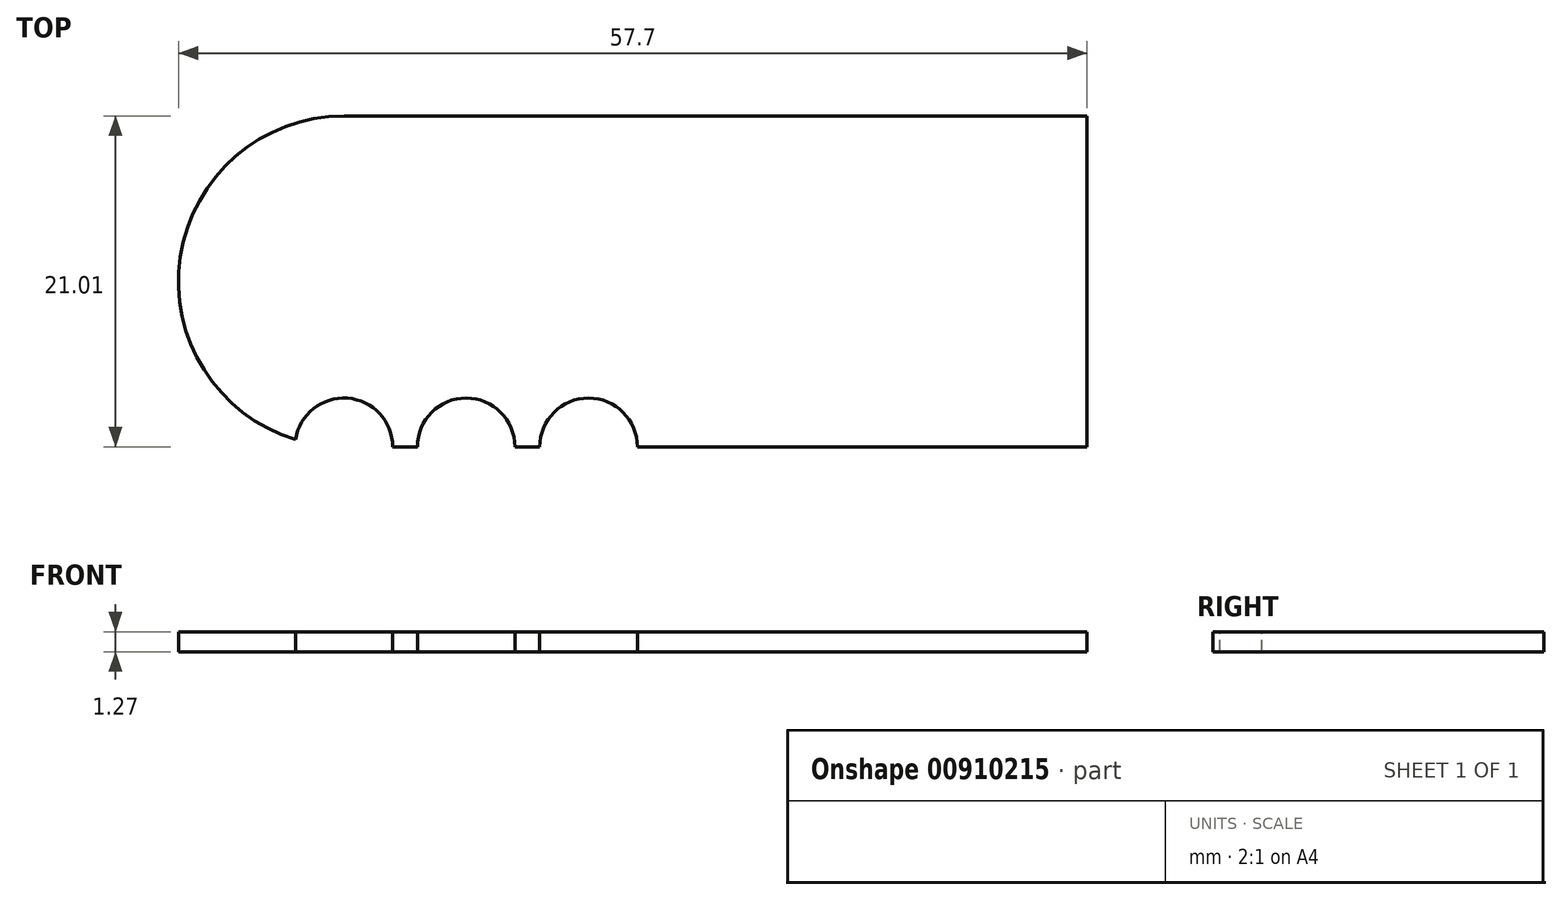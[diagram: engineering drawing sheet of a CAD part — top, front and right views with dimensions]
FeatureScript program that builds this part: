
annotation { "Feature Type Name" : "Feature", "Feature Type Description" : "" }
export const myFeature = defineFeature(function(context is Context, id is Id, definition is map)
    precondition{}
    {
        {
            var Q0;
            Q0=qCreatedBy(makeId("Top.planeOp"),FACE);
            var sketch = newSketch(context, id + "F0", { "sketchPlane" : qUnion([Q0])});
            skLineSegment(sketch, "E0.bottom", {"start": v(-3.6, 16.26) * mm, "end": v(43.6, 16.26) * mm});
            skLineSegment(sketch, "E0.top", {"start": v(-3.6, -4.75) * mm, "end": v(43.6, -4.75) * mm});
            skLineSegment(sketch, "E0.left", {"start": v(-3.6, 16.26) * mm, "end": v(-3.6, -4.75) * mm});
            skLineSegment(sketch, "E0.right", {"start": v(43.6, 16.26) * mm, "end": v(43.6, -4.75) * mm});
            skArc(sketch, "E1", {"start": v(-3.6, 16.26) * mm, "mid": v(-14.1, 5.76) * mm, "end": v(-3.6, -4.75) * mm});
            skSolve(sketch);
        }
        {
            var Q0;
            Q0=makeQuery(id+"F0.imprint","IMPRINT",FACE,{"disambiguationData":[TD([[makeQuery(id+"F0.imprint","IMPRINT",EDGE,{"derivedFrom":sQuery(id+"F0.wireOp",EDGE,"E0.bottom")}),-1.0]])]});
            var Q1;
            Q1=makeQuery(id+"F0.imprint","IMPRINT",FACE,{"disambiguationData":[TD([[makeQuery(id+"F0.imprint","IMPRINT",EDGE,{"derivedFrom":sQuery(id+"F0.wireOp",EDGE,"E0.left")}),-1.0]])]});
            extrude(context, id + "F1", {"entities" : qUnion([Q0, Q1]), "depth" : 1.27 * mm, "offsetDistance" : 25.4 * mm});
        }
        {
            var Q0;
            Q0=makeQuery(id+"F1.opExtrude","CAP_FACE",FACE,{"disambiguationData":[OSD([sQuery(id+"F0.wireOp",EDGE,"E0.bottom"),sQuery(id+"F0.wireOp",EDGE,"E0.top"),sQuery(id+"F0.wireOp",EDGE,"E0.right"),sQuery(id+"F0.wireOp",EDGE,"E1")])],"isStart":false});
            var sketch = newSketch(context, id + "F2", { "sketchPlane" : qUnion([Q0])});
            skCircle(sketch, "E2", {"center": v(-3.6, -4.75) * mm, "radius": 3.1 * mm});
            skCircle(sketch, "E3", {"center": v(4.17, -4.75) * mm, "radius": 3.1 * mm});
            skCircle(sketch, "E4", {"center": v(11.94, -4.75) * mm, "radius": 3.1 * mm});
            skSolve(sketch);
        }
        {
            var Q0;
            {var subQ0=sQuery(id+"F2.wireOp",EDGE,"E3");var subQ1=makeQuery(id+"F1.opExtrude","CAP_EDGE",EDGE,{"disambiguationData":[OSD([sQuery(id+"F0.wireOp",EDGE,"E0.top")])],"isStart":false});var subQ2=makeQuery(id+"F2.imprint","INTERSECT",VERTEX,{"disambiguationData":[OD(0.0)],"derivedFrom":[subQ1,subQ0]});Q0=makeQuery(id+"F2.imprint","IMPRINT",FACE,{"disambiguationData":[TD([[makeQuery(id+"F2.imprint","IMPRINT",EDGE,{"disambiguationData":[TD([[subQ2,-1.0]])],"derivedFrom":subQ0}),1.0]])]});}
            var Q1;
            {var subQ0=sQuery(id+"F2.wireOp",EDGE,"E3");var subQ1=makeQuery(id+"F1.opExtrude","CAP_EDGE",EDGE,{"disambiguationData":[OSD([sQuery(id+"F0.wireOp",EDGE,"E0.top")])],"isStart":false});var subQ2=makeQuery(id+"F2.imprint","INTERSECT",VERTEX,{"disambiguationData":[OD(0.0)],"derivedFrom":[subQ1,subQ0]});Q1=makeQuery(id+"F2.imprint","IMPRINT",FACE,{"disambiguationData":[TD([[makeQuery(id+"F2.imprint","IMPRINT",EDGE,{"disambiguationData":[TD([[subQ2,1.0]])],"derivedFrom":subQ0}),1.0]])]});}
            var Q2;
            {var subQ0=sQuery(id+"F2.wireOp",EDGE,"E2");var subQ1=makeQuery(id+"F1.opExtrude","CAP_EDGE",EDGE,{"disambiguationData":[OSD([sQuery(id+"F0.wireOp",EDGE,"E1")])],"isStart":false});var subQ2=makeQuery(id+"F2.imprint","INTERSECT",VERTEX,{"derivedFrom":[subQ1,subQ0]});Q2=makeQuery(id+"F2.imprint","IMPRINT",FACE,{"disambiguationData":[TD([[makeQuery(id+"F2.imprint","IMPRINT",EDGE,{"disambiguationData":[TD([[subQ2,1.0]])],"derivedFrom":subQ0}),1.0]])]});}
            var Q3;
            {var subQ0=sQuery(id+"F2.wireOp",EDGE,"E4");var subQ1=makeQuery(id+"F1.opExtrude","CAP_EDGE",EDGE,{"disambiguationData":[OSD([sQuery(id+"F0.wireOp",EDGE,"E0.top")])],"isStart":false});var subQ2=makeQuery(id+"F2.imprint","INTERSECT",VERTEX,{"disambiguationData":[OD(0.0)],"derivedFrom":[subQ1,subQ0]});Q3=makeQuery(id+"F2.imprint","IMPRINT",FACE,{"disambiguationData":[TD([[makeQuery(id+"F2.imprint","IMPRINT",EDGE,{"disambiguationData":[TD([[subQ2,-1.0]])],"derivedFrom":subQ0}),1.0]])]});}
            extrude(context, id + "F3", {"entities" : qUnion([Q0, Q1, Q2, Q3]), "operationType" : NewBodyOperationType.REMOVE, "oppositeDirection" : true, "depth" : 25.4 * mm, "offsetDistance" : 25.4 * mm});
        }
    });
